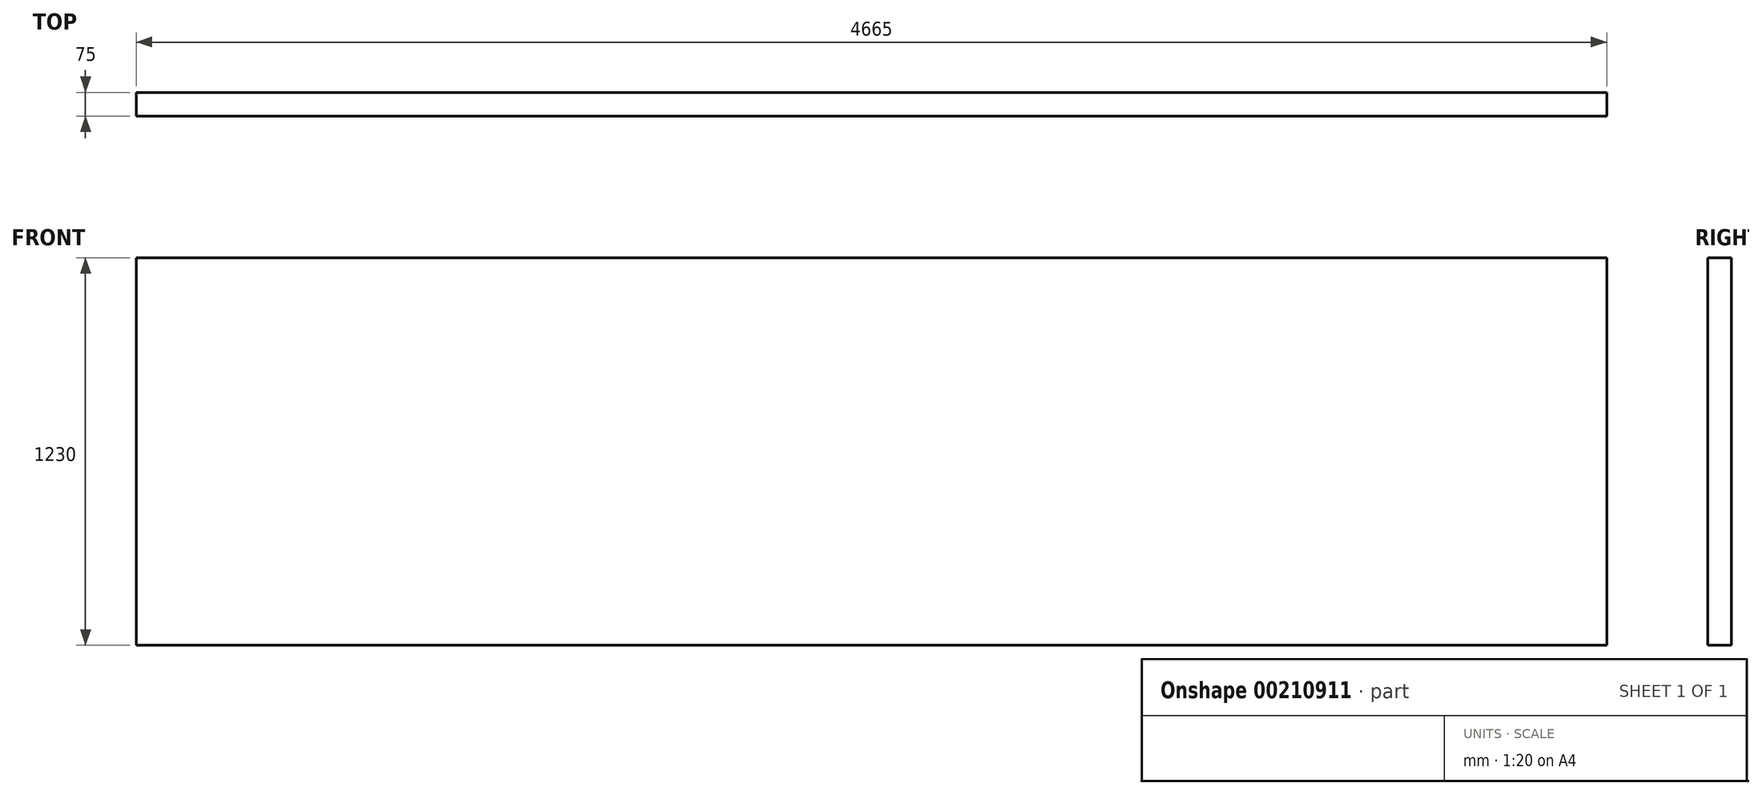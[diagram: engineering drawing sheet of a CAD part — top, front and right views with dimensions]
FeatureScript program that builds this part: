
annotation { "Feature Type Name" : "Feature", "Feature Type Description" : "" }
export const myFeature = defineFeature(function(context is Context, id is Id, definition is map)
    precondition{}
    {
        {
            var Q0;
            Q0=qCreatedBy(makeId("Front.planeOp"),FACE);
            var sketch = newSketch(context, id + "F0", { "sketchPlane" : qUnion([Q0])});
            skLineSegment(sketch, "E0.bottom", {"start": v(0, 0) * mm, "end": v(4665, 0) * mm});
            skLineSegment(sketch, "E0.right", {"start": v(4665, 0) * mm, "end": v(4665, 1230) * mm});
            skLineSegment(sketch, "E1", {"start": v(0, 1230) * mm, "end": v(4665, 1230) * mm});
            skLineSegment(sketch, "E2", {"start": v(0, 0) * mm, "end": v(0, 1230) * mm});
            skSolve(sketch);
        }
        {
            var Q0;
            Q0=makeQuery(id+"F0.imprint","IMPRINT",FACE,{"disambiguationData":[TD([[makeQuery(id+"F0.imprint","IMPRINT",EDGE,{"derivedFrom":sQuery(id+"F0.wireOp",EDGE,"E0.bottom")}),1.0]])]});
            extrude(context, id + "F1", {"entities" : qUnion([Q0]), "depth" : 75 * mm});
        }
    });
